# Revit family: 1503a_lightowl_dia
name_source: partatom
category: Communication Devices
units: mm (PartAtom-declared; Revit-internal decimal feet)

## family parameters
Cut with Voids When Loaded = No
Host = Face
Maintain Annotation Orientation = No
OmniClass Number = 23.85.80.11.27
OmniClass Title = Lighting Controls
Part Type = Normal
Room Calculation Point = No
Round Connector Dimension = Use Diameter
Shared = Yes

## types (1)
- 1503a_lightowl_dia
    Assembly Code = D5090
    Certifications = UL and cUL listed
    Default Elevation = 48 "
    Description = The LightOWL Dual Technology Passive Infrared and Acoustic Sensorr combines
passive infrared (PIR) and acoustic (sound-activated) technologies to turn lighting
on and off based on occupancy. This sensor features  Controls' patented
IntelliDAPT® technology, which makes all the sensor adjustments automatically.
    Feartures = IntelliDAPT self-adaptive technology—no manual adjustment required 
All-digital dual technology (passive infrared [PIR] and acoustic) sensor
Non-volatile memory for sensor settings
1,600 square-foot coverage area 
Optional relay and photocell control 
Optional Quick-to-Install (QTI) connector 
UL and cUL listed
California Title 24 compliant
Five-year limited warranty
Low voltage device: 24 Vdc
    Housing Material = Paint -  Matte White
    Manufacturer = NX Lighting Controls
    Model = NX Ceiling Mount Occupancy Sensors employ Passive Infrared
and Ultrasonic sensing technologies to turn lighting on and off based
on occupancy
    Power Requirements = 24VDC, 33 mA (uses UVPP and MP-Series power pack—not included)
    Sensing Element = Metal-Nickel
    Type Comments = Wall Mount Occupancy Sensors
    URL = https://www.currentlighting.com
    Warranty = 5-Years Warranty

## geometry (parser evidence)
native form markers: Sweep x5
no freeform markers — native parametric forms only
